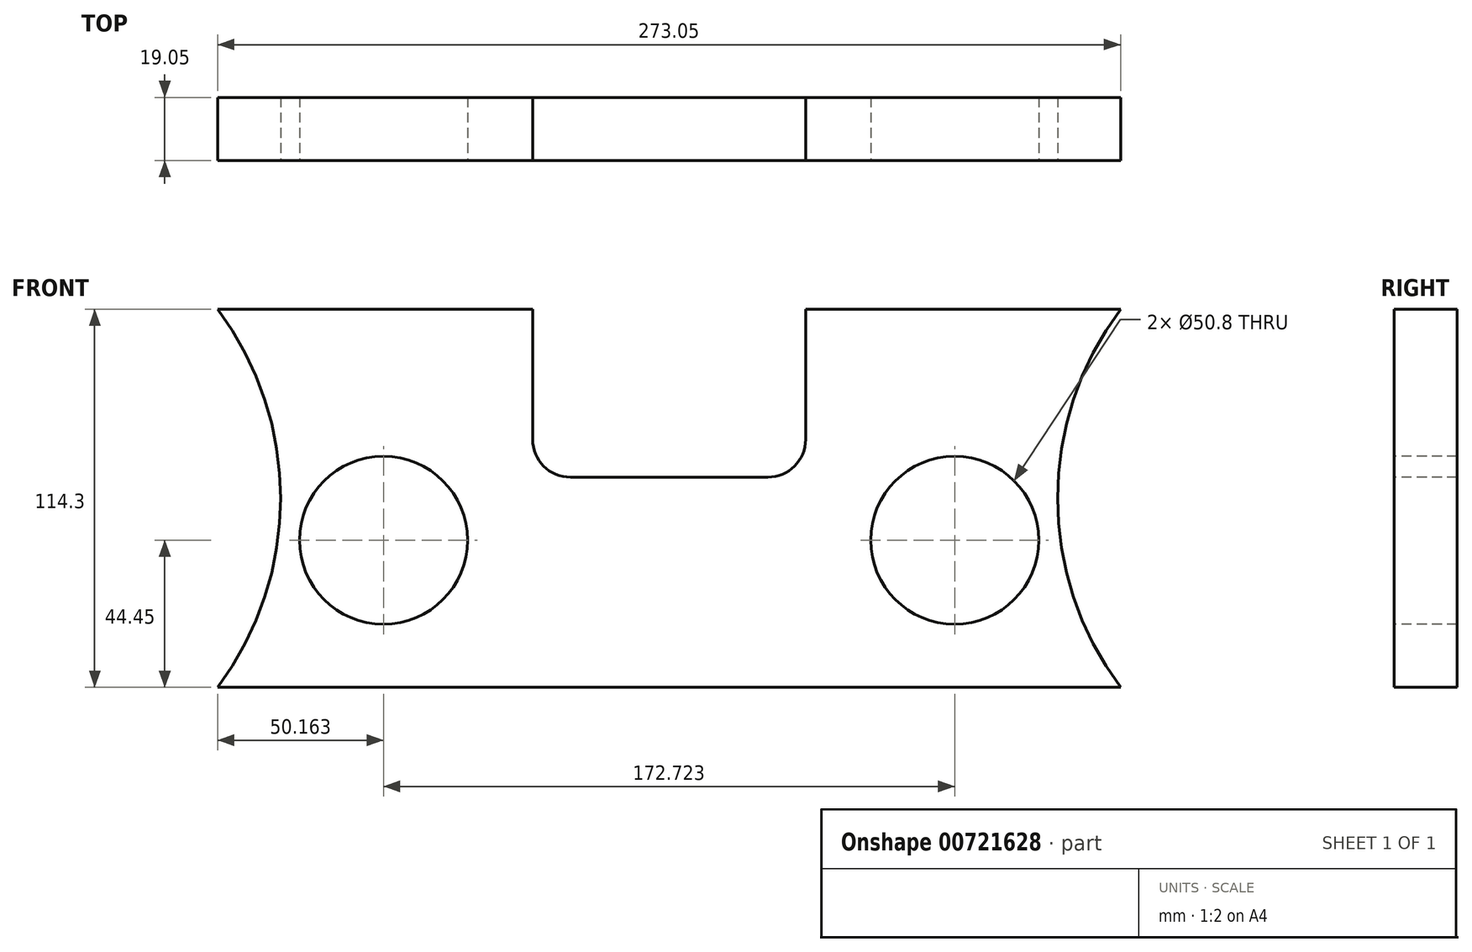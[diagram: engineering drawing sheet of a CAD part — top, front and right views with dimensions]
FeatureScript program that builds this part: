
annotation { "Feature Type Name" : "Feature", "Feature Type Description" : "" }
export const myFeature = defineFeature(function(context is Context, id is Id, definition is map)
    precondition{}
    {
        {
            var Q0;
            Q0=qCreatedBy(makeId("Front.planeOp"),FACE);
            var sketch = newSketch(context, id + "F0", { "sketchPlane" : qUnion([Q0])});
            skLineSegment(sketch, "E0.bottom", {"start": v(0, 0) * mm, "end": v(273.05, 0) * mm});
            skLineSegment(sketch, "E0.top", {"start": v(0, 114.3) * mm, "end": v(273.05, 114.3) * mm});
            skLineSegment(sketch, "E0.left", {"start": v(0, 0) * mm, "end": v(0, 114.3) * mm});
            skLineSegment(sketch, "E0.right", {"start": v(273.05, 0) * mm, "end": v(273.05, 114.3) * mm});
            skSolve(sketch);
        }
        {
            var Q0;
            Q0=makeQuery(id+"F0.imprint","IMPRINT",FACE,{"disambiguationData":[TD([[makeQuery(id+"F0.imprint","IMPRINT",EDGE,{"derivedFrom":sQuery(id+"F0.wireOp",EDGE,"E0.bottom")}),1.0]])]});
            extrude(context, id + "F1", {"entities" : qUnion([Q0]), "depth" : 19.05 * mm, "offsetDistance" : 25.4 * mm});
        }
        {
            var Q0;
            Q0=makeQuery(id+"F1.opExtrude","CAP_FACE",FACE,{"disambiguationData":[OSD([sQuery(id+"F0.wireOp",EDGE,"E0.bottom"),sQuery(id+"F0.wireOp",EDGE,"E0.top"),sQuery(id+"F0.wireOp",EDGE,"E0.left"),sQuery(id+"F0.wireOp",EDGE,"E0.right")])],"isStart":false});
            var sketch = newSketch(context, id + "F2", { "sketchPlane" : qUnion([Q0])});
            skArc(sketch, "E1", {"start": v(0, 0) * mm, "mid": v(19.05, 57.15) * mm, "end": v(0, 114.3) * mm});
            skArc(sketch, "E2", {"start": v(273.05, 114.3) * mm, "mid": v(254, 57.15) * mm, "end": v(273.05, 0) * mm});
            skSolve(sketch);
        }
        {
            var Q0;
            Q0=makeQuery(id+"F2.imprint","IMPRINT",FACE,{"disambiguationData":[TD([[makeQuery(id+"F2.imprint","IMPRINT",EDGE,{"derivedFrom":sQuery(id+"F2.wireOp",EDGE,"E1")}),1.0]])]});
            var Q1;
            Q1=makeQuery(id+"F2.imprint","IMPRINT",FACE,{"disambiguationData":[TD([[makeQuery(id+"F2.imprint","IMPRINT",EDGE,{"derivedFrom":sQuery(id+"F2.wireOp",EDGE,"E2")}),1.0]])]});
            extrude(context, id + "F3", {"entities" : qUnion([Q0, Q1]), "operationType" : NewBodyOperationType.REMOVE, "oppositeDirection" : true, "depth" : 25.4 * mm, "offsetDistance" : 25.4 * mm});
        }
        {
            var Q0;
            Q0=makeQuery(id+"F1.opExtrude","CAP_FACE",FACE,{"disambiguationData":[OSD([sQuery(id+"F0.wireOp",EDGE,"E0.bottom"),sQuery(id+"F0.wireOp",EDGE,"E0.top"),sQuery(id+"F0.wireOp",EDGE,"E0.left"),sQuery(id+"F0.wireOp",EDGE,"E0.right")])],"isStart":false});
            var sketch = newSketch(context, id + "F4", { "sketchPlane" : qUnion([Q0])});
            skLineSegment(sketch, "E3", {"start": v(95.25, 114.3) * mm, "end": v(95.25, 63.5) * mm});
            skLineSegment(sketch, "E4", {"start": v(95.25, 63.5) * mm, "end": v(177.8, 63.5) * mm});
            skLineSegment(sketch, "E5", {"start": v(177.8, 63.5) * mm, "end": v(177.8, 114.3) * mm});
            skCircle(sketch, "E6", {"center": v(50.16, 44.45) * mm, "radius": 25.4 * mm});
            skCircle(sketch, "E7", {"center": v(222.89, 44.45) * mm, "radius": 25.4 * mm});
            skCircle(sketch, "E8", {"center": v(106.68, 74.93) * mm, "radius": 11.43 * mm});
            skCircle(sketch, "E9", {"center": v(166.37, 74.93) * mm, "radius": 11.43 * mm});
            skSolve(sketch);
        }
        {
            var Q0;
            {var subQ1=makeQuery(id+"F1.opExtrude","CAP_EDGE",EDGE,{"disambiguationData":[OSD([sQuery(id+"F0.wireOp",EDGE,"E0.top")])],"isStart":false});var subQ9=sQuery(id+"F4.wireOp",EDGE,"E3");var subQ11=makeQuery(id+"F4.imprint","INTERSECT",VERTEX,{"derivedFrom":[subQ1,subQ9]});Q0=makeQuery(id+"F4.imprint","IMPRINT",FACE,{"disambiguationData":[TD([[makeQuery(id+"F4.imprint","IMPRINT",EDGE,{"disambiguationData":[TD([[subQ11,-1.0]])],"derivedFrom":subQ9}),1.0]])]});}
            var Q1;
            Q1=makeQuery(id+"F4.imprint","IMPRINT",FACE,{"disambiguationData":[TD([[makeQuery(id+"F4.imprint","IMPRINT",EDGE,{"derivedFrom":sQuery(id+"F4.wireOp",EDGE,"E6")}),1.0]])]});
            var Q2;
            Q2=makeQuery(id+"F4.imprint","IMPRINT",FACE,{"disambiguationData":[TD([[makeQuery(id+"F4.imprint","IMPRINT",EDGE,{"derivedFrom":sQuery(id+"F4.wireOp",EDGE,"E7")}),1.0]])]});
            var Q3;
            {var subQ0=sQuery(id+"F4.wireOp",EDGE,"E9");var subQ1=makeQuery(id+"F4.imprint","INTERSECT",VERTEX,{"derivedFrom":[sQuery(id+"F4.wireOp",EDGE,"E4"),subQ0]});Q3=makeQuery(id+"F4.imprint","IMPRINT",FACE,{"disambiguationData":[TD([[makeQuery(id+"F4.imprint","IMPRINT",EDGE,{"disambiguationData":[TD([[subQ1,1.0]])],"derivedFrom":subQ0}),1.0]])]});}
            var Q4;
            {var subQ0=sQuery(id+"F4.wireOp",EDGE,"E8");var subQ1=makeQuery(id+"F4.imprint","INTERSECT",VERTEX,{"derivedFrom":[sQuery(id+"F4.wireOp",EDGE,"E3"),subQ0]});Q4=makeQuery(id+"F4.imprint","IMPRINT",FACE,{"disambiguationData":[TD([[makeQuery(id+"F4.imprint","IMPRINT",EDGE,{"disambiguationData":[TD([[subQ1,-1.0]])],"derivedFrom":subQ0}),1.0]])]});}
            extrude(context, id + "F5", {"entities" : qUnion([Q0, Q1, Q2, Q3, Q4]), "operationType" : NewBodyOperationType.REMOVE, "oppositeDirection" : true, "depth" : 25.4 * mm, "offsetDistance" : 25.4 * mm});
        }
    });
